# Revit family: Electronics_Masking-Generators_Biamp_Cambridge_Sound-Masking-Control-Module_QT-100
name_source: partatom
category: Communication Devices
units: mm (PartAtom-declared; Revit-internal decimal feet)

## family parameters
Cut with Voids When Loaded = No
Host = Face
Maintain Annotation Orientation = No
OmniClass Number = 23.85.10.11.11
OmniClass Title = Sound and Signal Devices
Part Type = Normal
Room Calculation Point = No
Round Connector Dimension = Use Diameter
Shared = No

## types (1)
- Qt 100
    Altitude = 0-6,600 ft (0-2000m) MSL
    Apparent Load = 72 VA
    Audio Inputs Number of Inputs = 1 (Stereo or Mono)
    Compliance = FCC Part 15B (USA), ETL Listed (USA and Canada), CE Marked (Europe), RoHS Directive (Europe), Green Spec Listed
    Connector Description = Captive Screw Terminal & Coax Power Plug (center pin positive); 120VAC 50/60Hz
    Connector Type = Captive Screw Terminal
    Current = 1 A
    Default Elevation = 48 "
    Depth = 0.88 "
    Description = QT® 100 Sound Masking Control Module
    Frequency Response Music/Paging = 200Hz to 10kHz
    Frequency Response Sound Masking = 200Hz to 6.3kHz
    Height = 3.5 "
    Housing Material = Biamp - Plastic - Black
    Humidity = 0-95% relative humidity (non-condensing)
    Included Accessories = ACT Hole Saw
    Input Connector = Captive Screw Terminal & Coax Power Plug (center pin positive)
    Input Impedance = 5kΩ
    Input Level = +4dBu (2VRMS max)
    Input Level Adjustment = 1dB steps
    Input Type = Contact Closure (Normally Open)
    Manufacturer = Biamp
    Masking Level Adjustment = 0.5dB steps
    Max Emitter Cabling Distance = 1000 feet (300m) per cable run
    Max Emitter/Device Capacity = 60 Qt Emitters or Room Controls per cable run
    Maximum Masking SPL = 60dBA
    Maximum Music/Paging SPL = 62dBA
    Minimum Masking SPL = 30dBA
    Minimum Output Impedance = 2Ω (per channel)
    Model = Qt 100
    Number of Masking Zones = 1 (2 cable runs per zone)
    Number of Non-Correlated Masking Sources = 4
    Number of Poles = 1
    Number of Remote Control Inputs = 1
    Number of Remote Control Outputs = 1
    Output Connections = 2 RJ-45
    Power Factor = 1
    Product Documentation Link = https://downloads.biamp.com
    Product Page URL = https://www.biamp.com
    Product data url = https://www.bimobject.com
    Remote Control = Captive Screw Terminal; Logic Status (5VDC)
    Temperature Range = 40 - 90° F (4 – 32° C)
    URL = https://www.biamp.com
    Voltage = 120 V
    Weight = 0.38 lbf
    Width = 7 "

## geometry (parser evidence)
native form markers: Sweep x2
no freeform markers — native parametric forms only
